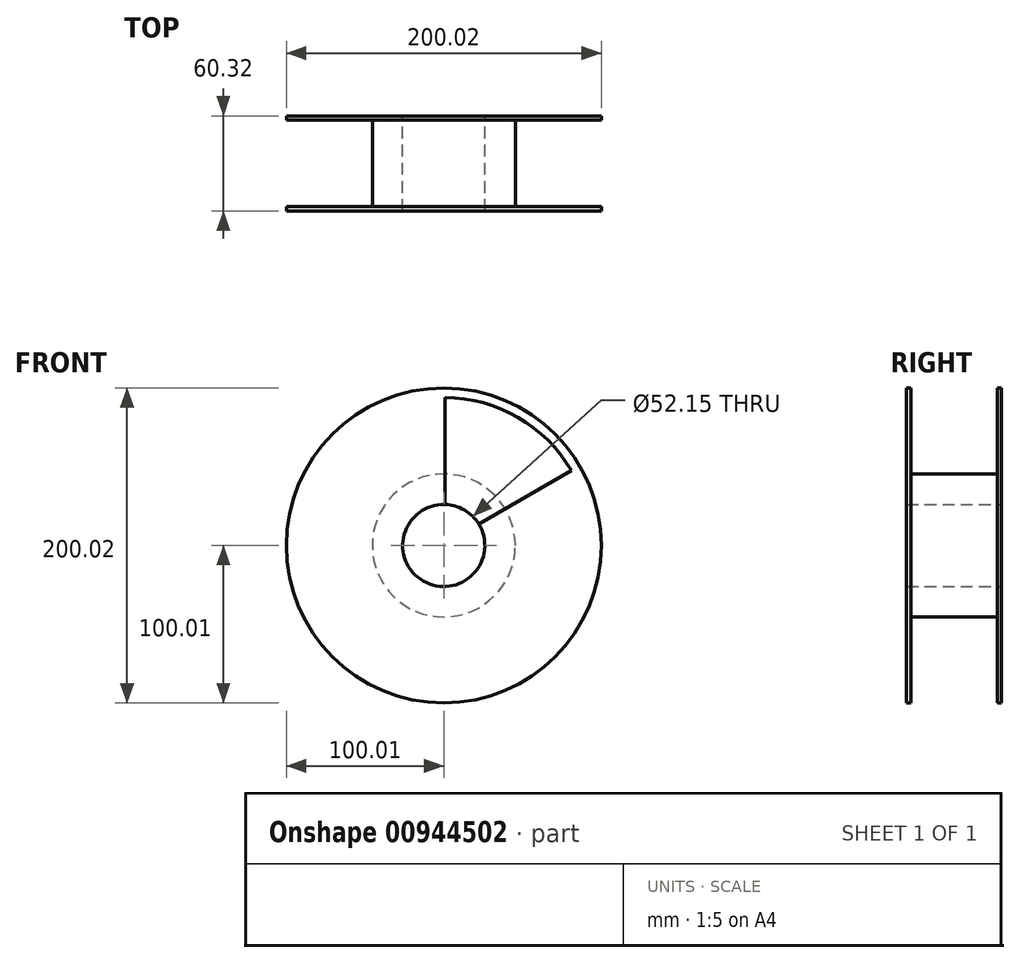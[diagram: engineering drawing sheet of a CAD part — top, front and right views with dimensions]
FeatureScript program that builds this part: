
annotation { "Feature Type Name" : "Feature", "Feature Type Description" : "" }
export const myFeature = defineFeature(function(context is Context, id is Id, definition is map)
    precondition{}
    {
        {
            var Q0;
            Q0=qCreatedBy(makeId("Front.planeOp"),FACE);
            var sketch = newSketch(context, id + "F0", { "sketchPlane" : qUnion([Q0])});
            skCircle(sketch, "E0", {"center": v(0, 0) * mm, "radius": 100.01 * mm});
            skCircle(sketch, "E1", {"center": v(0, 0) * mm, "radius": 26.07 * mm});
            skSolve(sketch);
        }
        {
            var Q0;
            Q0=qSketchRegion(id+"F0",true);
            extrude(context, id + "F1", {"entities" : qUnion([Q0]), "endBound" : BoundingType.SYMMETRIC, "depth" : 60.32 * mm, "offsetDistance" : 25 * mm});
        }
        {
            var Q0;
            Q0=qCreatedBy(makeId("Front.planeOp"),FACE);
            cPlane(context, id + "F2", {"entities" : qUnion([Q0]), "cplaneType" : CPlaneType.OFFSET, "offset" : 30.18 * mm, "width" : 150 * mm, "height" : 150 * mm});
        }
        {
            var Q0;
            Q0=qCreatedBy(makeId("Front.planeOp"),FACE);
            var sketch = newSketch(context, id + "F3", { "sketchPlane" : qUnion([Q0])});
            skCircle(sketch, "E2", {"center": v(0, 0) * mm, "radius": 100.01 * mm});
            skCircle(sketch, "E3", {"center": v(0, 0) * mm, "radius": 45.4 * mm});
            skSolve(sketch);
        }
        {
            var Q0;
            Q0=qSketchRegion(id+"F3",true);
            extrude(context, id + "F4", {"entities" : qUnion([Q0]), "operationType" : NewBodyOperationType.REMOVE, "endBound" : BoundingType.SYMMETRIC, "oppositeDirection" : true, "depth" : 55.02 * mm, "offsetDistance" : 25 * mm});
        }
        {
            var Q0;
            Q0=qCreatedBy(id+"F2.planeOp",FACE);
            var sketch = newSketch(context, id + "F5", { "sketchPlane" : qUnion([Q0])});
            skCircle(sketch, "E4.cCircle", {"center": v(0, 0) * mm, "radius": 100.01 * mm, "construction": true});
            skLineSegment(sketch, "E4.0", {"start": v(86.61, 50) * mm, "end": v(86.61, -50) * mm, "construction": true});
            skLineSegment(sketch, "E4.1", {"start": v(86.61, -50) * mm, "end": v(0, -100.01) * mm, "construction": true});
            skLineSegment(sketch, "E4.2", {"start": v(0, -100.01) * mm, "end": v(-86.61, -50) * mm, "construction": true});
            skLineSegment(sketch, "E4.3", {"start": v(-86.61, -50) * mm, "end": v(-86.61, 50) * mm, "construction": true});
            skLineSegment(sketch, "E4.4", {"start": v(-86.61, 50) * mm, "end": v(0, 100.01) * mm, "construction": true});
            skLineSegment(sketch, "E4.5", {"start": v(0, 100.01) * mm, "end": v(86.61, 50) * mm, "construction": true});
            skLineSegment(sketch, "E5", {"start": v(0, 0) * mm, "end": v(0, 100.01) * mm, "construction": true});
            skLineSegment(sketch, "E6", {"start": v(0, 0) * mm, "end": v(86.61, 50) * mm, "construction": true});
            skLineSegment(sketch, "E7", {"start": v(0, 0) * mm, "end": v(86.61, -50) * mm, "construction": true});
            skLineSegment(sketch, "E8", {"start": v(0, 0) * mm, "end": v(0, -100.01) * mm, "construction": true});
            skLineSegment(sketch, "E9", {"start": v(0, 0) * mm, "end": v(-86.61, -50) * mm, "construction": true});
            skLineSegment(sketch, "E10", {"start": v(0, 0) * mm, "end": v(-86.61, 50) * mm, "construction": true});
            skLineSegment(sketch, "E11", {"start": v(0.7, 1.21) * mm, "end": v(0.7, 94.02) * mm});
            skLineSegment(sketch, "E12", {"start": v(0.7, 1.21) * mm, "end": v(81.07, 47.61) * mm});
            skArc(sketch, "E13", {"start": v(81.07, 47.61) * mm, "mid": v(47, 81.42) * mm, "end": v(0.7, 94.02) * mm});
            skLineSegment(sketch, "E14", {"start": v(18.73, 42.45) * mm, "end": v(23.73, 51.11) * mm, "construction": true});
            skLineSegment(sketch, "E15", {"start": v(23.73, 51.11) * mm, "end": v(32.4, 46.11) * mm, "construction": true});
            skLineSegment(sketch, "E16", {"start": v(32.4, 46.11) * mm, "end": v(27.4, 37.45) * mm, "construction": true});
            skLineSegment(sketch, "E17", {"start": v(27.4, 37.45) * mm, "end": v(18.73, 42.45) * mm, "construction": true});
            skLineSegment(sketch, "E18", {"start": v(0, 0) * mm, "end": v(23.07, 39.95) * mm, "construction": true});
            skLineSegment(sketch, "E19", {"start": v(28.07, 48.61) * mm, "end": v(47, 81.42) * mm, "construction": true});
            skSolve(sketch);
        }
        {
            var Q0;
            Q0=qSketchRegion(id+"F5",true);
            extrude(context, id + "F6", {"entities" : qUnion([Q0]), "operationType" : NewBodyOperationType.REMOVE, "oppositeDirection" : true, "depth" : .25 * mm, "offsetDistance" : 25 * mm});
        }
        {
            var Q0;
            Q0=qCreatedBy(makeId("Top.planeOp"),FACE);
            var sketch = newSketch(context, id + "F7", { "sketchPlane" : qUnion([Q0])});
            skCircle(sketch, "E20", {"center": v(-46.3, -26.63) * mm, "radius": 0.88 * mm});
            skLineSegment(sketch, "E21", {"start": v(0, -26.63) * mm, "end": v(-46.3, -26.63) * mm, "construction": true});
            skSolve(sketch);
        }
    });
